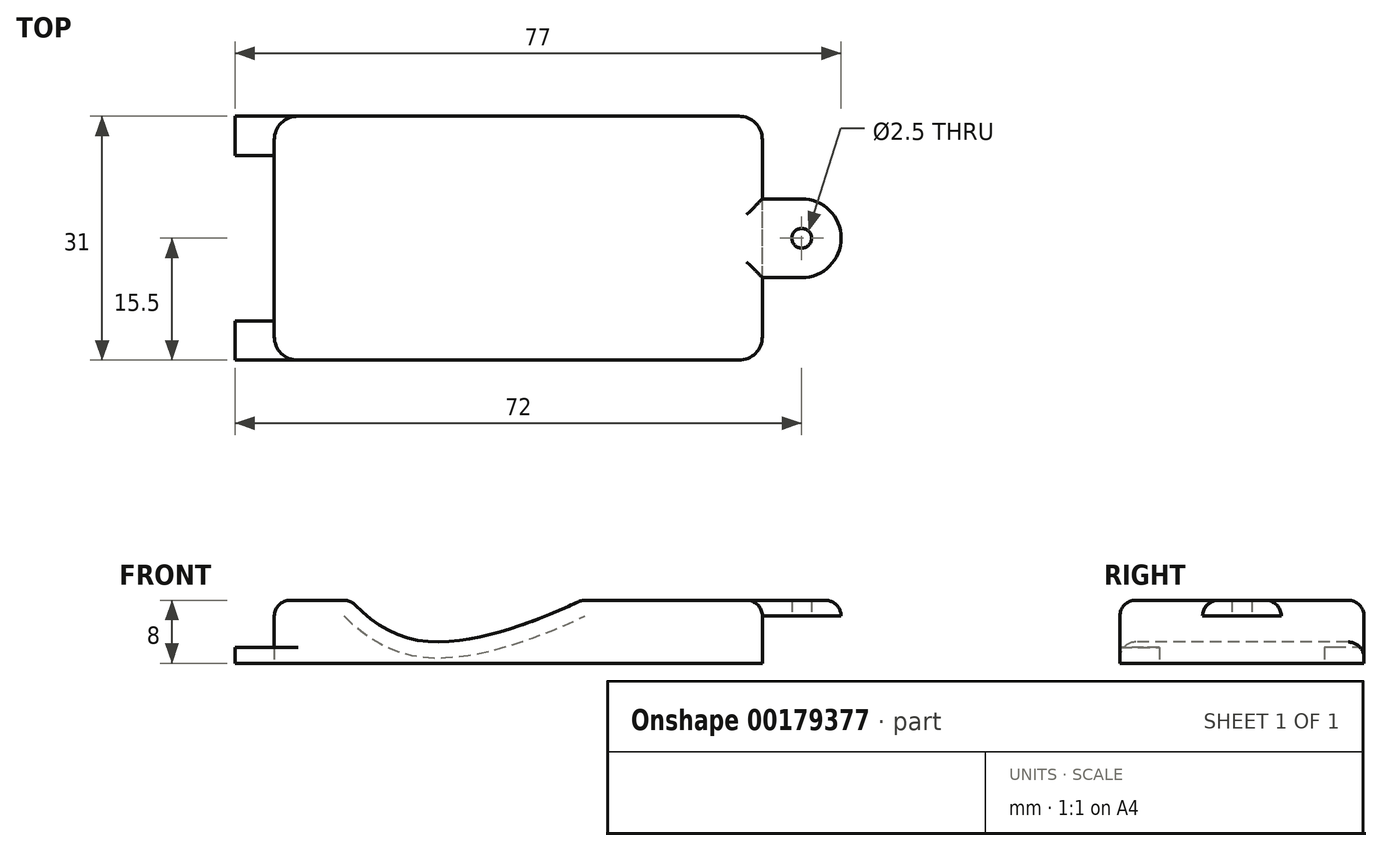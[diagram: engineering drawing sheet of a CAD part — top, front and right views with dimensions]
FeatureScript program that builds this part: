
annotation { "Feature Type Name" : "Feature", "Feature Type Description" : "" }
export const myFeature = defineFeature(function(context is Context, id is Id, definition is map)
    precondition{}
    {
        {
            var Q0;
            Q0=qCreatedBy(makeId("Top.planeOp"),FACE);
            var sketch = newSketch(context, id + "F0", { "sketchPlane" : qUnion([Q0])});
            skLineSegment(sketch, "E0.bottom", {"start": v(28, -15.5) * mm, "end": v(-31, -15.5) * mm});
            skLineSegment(sketch, "E0.top", {"start": v(28, 15.5) * mm, "end": v(-31, 15.5) * mm});
            skLineSegment(sketch, "E0.left", {"start": v(31, -12.5) * mm, "end": v(31, 12.5) * mm});
            skLineSegment(sketch, "E0.right", {"start": v(-31, -15.5) * mm, "end": v(-31, 15.5) * mm});
            skPoint(sketch, "E0.middle", {"position": v(0, 0) * mm});
            skLineSegment(sketch, "E1", {"start": v(48.88, 0) * mm, "end": v(-42.9, 0) * mm, "construction": true});
            skLineSegment(sketch, "E2.bottom", {"start": v(31, -5) * mm, "end": v(36, -5) * mm});
            skLineSegment(sketch, "E2.top", {"start": v(31, 5) * mm, "end": v(36, 5) * mm});
            skLineSegment(sketch, "E2.left", {"start": v(31, -5) * mm, "end": v(31, 5) * mm});
            skLineSegment(sketch, "E2.right", {"start": v(41, 0) * mm, "end": v(41, 0) * mm});
            skLineSegment(sketch, "E3.bottom", {"start": v(-31, 15.5) * mm, "end": v(-36, 15.5) * mm});
            skLineSegment(sketch, "E3.top", {"start": v(-31, 10.5) * mm, "end": v(-36, 10.5) * mm});
            skLineSegment(sketch, "E3.left", {"start": v(-31, 15.5) * mm, "end": v(-31, 10.5) * mm});
            skLineSegment(sketch, "E3.right", {"start": v(-36, 15.5) * mm, "end": v(-36, 10.5) * mm});
            skLineSegment(sketch, "E4.MirrorCS", {"start": v(-31, -10.5) * mm, "end": v(-36, -10.5) * mm});
            skLineSegment(sketch, "E5.MirrorCS", {"start": v(-36, -15.5) * mm, "end": v(-36, -10.5) * mm});
            skLineSegment(sketch, "E6.MirrorCS", {"start": v(-31, -15.5) * mm, "end": v(-36, -15.5) * mm});
            skPoint(sketch, "E7.visualSharp", {"position": v(41, 5) * mm});
            skArc(sketch, "E7.filletArc", {"start": v(41, 0) * mm, "mid": v(39.54, 3.54) * mm, "end": v(36, 5) * mm});
            skPoint(sketch, "E8.visualSharp", {"position": v(41, -5) * mm});
            skArc(sketch, "E8.filletArc", {"start": v(36, -5) * mm, "mid": v(39.54, -3.54) * mm, "end": v(41, 0) * mm});
            skPoint(sketch, "E9.visualSharp", {"position": v(31, 15.5) * mm});
            skArc(sketch, "E9.filletArc", {"start": v(31, 12.5) * mm, "mid": v(30.12, 14.62) * mm, "end": v(28, 15.5) * mm});
            skPoint(sketch, "E10.visualSharp", {"position": v(31, -15.5) * mm});
            skArc(sketch, "E10.filletArc", {"start": v(28, -15.5) * mm, "mid": v(30.12, -14.62) * mm, "end": v(31, -12.5) * mm});
            skCircle(sketch, "E11", {"center": v(36, 0) * mm, "radius": 1.25 * mm});
            skSolve(sketch);
        }
        {
            var Q0;
            Q0=makeQuery(id+"F0.imprint","IMPRINT",FACE,{"disambiguationData":[TD([[makeQuery(id+"F0.imprint","IMPRINT",EDGE,{"derivedFrom":sQuery(id+"F0.wireOp",EDGE,"E3.bottom")}),1.0]])]});
            var Q1;
            {var subQ3=sQuery(id+"F0.wireOp",EDGE,"E0.bottom");Q1=makeQuery(id+"F0.imprint","IMPRINT",FACE,{"disambiguationData":[TD([[makeQuery(id+"F0.imprint","IMPRINT",EDGE,{"derivedFrom":subQ3}),-1.0]])]});}
            var Q2;
            {var subQ2=sQuery(id+"F0.wireOp",EDGE,"E4.MirrorCS");Q2=makeQuery(id+"F0.imprint","IMPRINT",FACE,{"disambiguationData":[TD([[makeQuery(id+"F0.imprint","IMPRINT",EDGE,{"derivedFrom":subQ2}),1.0]])]});}
            extrude(context, id + "F1", {"entities" : qUnion([Q0, Q1, Q2]), "depth" : 2 * mm});
        }
        {
            var Q0;
            Q0=makeQuery(id+"F0.imprint","IMPRINT",FACE,{"disambiguationData":[TD([[makeQuery(id+"F0.imprint","IMPRINT",EDGE,{"derivedFrom":sQuery(id+"F0.wireOp",EDGE,"E2.bottom")}),1.0]])]});
            var Q1;
            {var subQ3=sQuery(id+"F0.wireOp",EDGE,"E0.bottom");Q1=makeQuery(id+"F0.imprint","IMPRINT",FACE,{"disambiguationData":[TD([[makeQuery(id+"F0.imprint","IMPRINT",EDGE,{"derivedFrom":subQ3}),-1.0]])]});}
            extrude(context, id + "F2", {"entities" : qUnion([Q0, Q1]), "operationType" : NewBodyOperationType.ADD, "depth" : 8 * mm});
        }
        {
            var Q0;
            Q0=makeQuery(id+"F0.imprint","IMPRINT",FACE,{"disambiguationData":[TD([[makeQuery(id+"F0.imprint","IMPRINT",EDGE,{"derivedFrom":sQuery(id+"F0.wireOp",EDGE,"E2.bottom")}),1.0]])]});
            extrude(context, id + "F3", {"entities" : qUnion([Q0]), "operationType" : NewBodyOperationType.REMOVE, "depth" : 6 * mm});
        }
        {
            var Q0;
            {var subQ0=sQuery(id+"F0.wireOp",EDGE,"E0.bottom");Q0=makeQuery(id+"F2.boolean.opBoolean","MERGE",FACE,{"derivedFrom":[makeQuery(id+"F1.opExtrude","SWEPT_FACE",FACE,{"disambiguationData":[OSD([subQ0,sQuery(id+"F0.wireOp",EDGE,"E6.MirrorCS")])]}),makeQuery(id+"F2.opExtrude","SWEPT_FACE",FACE,{"disambiguationData":[OSD([subQ0])]})]});}
            var sketch = newSketch(context, id + "F4", { "sketchPlane" : qUnion([Q0])});
            skLineSegment(sketch, "E12", {"start": v(-21.3, 14.03) * mm, "end": v(-21.3, -8.42) * mm, "construction": true});
            skLineSegment(sketch, "E13", {"start": v(-12, 14.03) * mm, "end": v(-12, -8.42) * mm, "construction": true});
            skLineSegment(sketch, "E14", {"start": v(8, 14.03) * mm, "end": v(8, -8.42) * mm, "construction": true});
            skLineSegment(sketch, "E15", {"start": v(13.95, 2.8) * mm, "end": v(42.33, 2.46) * mm, "construction": true});
            skPoint(sketch, "E15.endSnap0", {"position": v(8, 2.8) * mm});
            skFitSpline(sketch, "E16", {"points": [v(-21.3, 8) * mm, v(-12, 2.8) * mm, v(8, 8) * mm], "startDerivative": vector(19.36, -20.15) * mm, "endDerivative": vector(38.26, 18.17) * mm});
            skLineSegment(sketch, "E17", {"start": v(-21.3, 8) * mm, "end": v(8, 8) * mm});
            skSolve(sketch);
        }
        {
            var Q0;
            Q0=makeQuery(id+"F2.opExtrude","SWEPT_EDGE",EDGE,{"disambiguationData":[OSD([sQuery(id+"F0.wireOp",EDGE,"E0.top"),sQuery(id+"F0.wireOp",EDGE,"E3.bottom"),sQuery(id+"F0.wireOp",EDGE,"E3.left")])]});
            var Q1;
            Q1=makeQuery(id+"F2.opExtrude","SWEPT_EDGE",EDGE,{"disambiguationData":[OSD([sQuery(id+"F0.wireOp",EDGE,"E0.bottom"),sQuery(id+"F0.wireOp",EDGE,"E0.right"),sQuery(id+"F0.wireOp",EDGE,"E6.MirrorCS")])]});
            fillet(context, id + "F5", {"entities" : qUnion([Q0, Q1]), "radius" : 3 * mm, "tangentPropagation" : true, "allowEdgeOverflow" : false});
        }
        {
            var Q0;
            Q0=makeQuery(id+"F4.imprint","IMPRINT",FACE,{"disambiguationData":[TD([[makeQuery(id+"F4.imprint","IMPRINT",EDGE,{"derivedFrom":sQuery(id+"F4.wireOp",EDGE,"E16")}),1.0]])]});
            extrude(context, id + "F6", {"entities" : qUnion([Q0]), "operationType" : NewBodyOperationType.REMOVE, "oppositeDirection" : true, "depth" : 50 * mm});
        }
        {
            var Q0;
            Q0=makeQuery(id+"F2.opExtrude","CAP_EDGE",EDGE,{"disambiguationData":[OSD([sQuery(id+"F0.wireOp",EDGE,"E2.bottom")])],"isStart":false});
            var Q1;
            Q1=makeQuery(id+"F2.opExtrude","CAP_EDGE",EDGE,{"disambiguationData":[OSD([sQuery(id+"F0.wireOp",EDGE,"E10.filletArc")])],"isStart":false});
            var Q2;
            Q2=makeQuery(id+"F6.boolean.opBoolean","COPY",FACE,{"derivedFrom":makeQuery(id+"F6.opExtrude","SWEPT_FACE",FACE,{"disambiguationData":[OSD([sQuery(id+"F4.wireOp",EDGE,"E16")])]})});
            var Q3;
            Q3=makeQuery(id+"F2.opExtrude","CAP_EDGE",EDGE,{"disambiguationData":[OSD([sQuery(id+"F0.wireOp",EDGE,"E2.top")])],"isStart":false});
            var Q4;
            {var subQ0=sQuery(id+"F0.wireOp",EDGE,"E0.left");Q4=makeQuery(id+"F2.opExtrude","CAP_EDGE",EDGE,{"disambiguationData":[OSD([subQ0]),TDD([makeQuery(id+"F0.imprint","IMPRINT",EDGE,{"disambiguationData":[TD([[makeQuery(id+"F0.imprint","INTERSECT",VERTEX,{"derivedFrom":[subQ0,sQuery(id+"F0.wireOp",EDGE,"E9.filletArc")]}),1.0]])],"derivedFrom":subQ0})])],"isStart":false});}
            var Q5;
            Q5=makeQuery(id+"F2.opExtrude","CAP_EDGE",EDGE,{"disambiguationData":[OSD([sQuery(id+"F0.wireOp",EDGE,"E9.filletArc")])],"isStart":false});
            var Q6;
            {var subQ0=sQuery(id+"F0.wireOp",EDGE,"E0.bottom");var subQ1=sQuery(id+"F0.wireOp",EDGE,"E0.right");var subQ3=sQuery(id+"F0.wireOp",EDGE,"E0.top");var subQ5=sQuery(id+"F0.wireOp",EDGE,"E3.left");Q6=makeQuery(id+"F6.boolean.opBoolean","SPLIT",FACE,{"disambiguationData":[TD([makeQuery(id+"F1.opExtrude","SWEPT_FACE",FACE,{"disambiguationData":[OSD([subQ1])]})])],"derivedFrom":makeQuery(id+"F2.opExtrude","CAP_FACE",FACE,{"disambiguationData":[OSD([subQ0,subQ3,sQuery(id+"F0.wireOp",EDGE,"E0.left"),subQ1,sQuery(id+"F0.wireOp",EDGE,"E2.bottom"),sQuery(id+"F0.wireOp",EDGE,"E2.top"),subQ5,sQuery(id+"F0.wireOp",EDGE,"E7.filletArc"),sQuery(id+"F0.wireOp",EDGE,"E8.filletArc"),sQuery(id+"F0.wireOp",EDGE,"E9.filletArc"),sQuery(id+"F0.wireOp",EDGE,"E10.filletArc"),sQuery(id+"F0.wireOp",EDGE,"E11")])],"isStart":false})});}
            var Q7;
            {var subQ0=sQuery(id+"F0.wireOp",EDGE,"E10.filletArc");var subQ1=sQuery(id+"F0.wireOp",EDGE,"E0.bottom");Q7=makeQuery(id+"F6.boolean.opBoolean","SPLIT",EDGE,{"disambiguationData":[TD([makeQuery(id+"F1.opExtrude","SWEPT_FACE",FACE,{"disambiguationData":[OSD([subQ0])]})])],"derivedFrom":makeQuery(id+"F2.opExtrude","CAP_EDGE",EDGE,{"disambiguationData":[OSD([subQ1])],"isStart":false})});}
            var Q8;
            {var subQ0=sQuery(id+"F0.wireOp",EDGE,"E0.left");Q8=makeQuery(id+"F2.opExtrude","CAP_EDGE",EDGE,{"disambiguationData":[OSD([subQ0]),TDD([makeQuery(id+"F0.imprint","IMPRINT",EDGE,{"disambiguationData":[TD([[makeQuery(id+"F0.imprint","INTERSECT",VERTEX,{"derivedFrom":[subQ0,sQuery(id+"F0.wireOp",EDGE,"E10.filletArc")]}),-1.0]])],"derivedFrom":subQ0})])],"isStart":false});}
            var Q9;
            Q9=makeQuery(id+"F2.opExtrude","CAP_EDGE",EDGE,{"disambiguationData":[OSD([sQuery(id+"F0.wireOp",EDGE,"E7.filletArc"),sQuery(id+"F0.wireOp",EDGE,"E8.filletArc")])],"isStart":false});
            var Q10;
            {var subQ0=sQuery(id+"F0.wireOp",EDGE,"E0.top");var subQ1=sQuery(id+"F0.wireOp",EDGE,"E9.filletArc");Q10=makeQuery(id+"F6.boolean.opBoolean","SPLIT",EDGE,{"disambiguationData":[TD([makeQuery(id+"F1.opExtrude","SWEPT_FACE",FACE,{"disambiguationData":[OSD([subQ1])]})])],"derivedFrom":makeQuery(id+"F2.opExtrude","CAP_EDGE",EDGE,{"disambiguationData":[OSD([subQ0])],"isStart":false})});}
            fillet(context, id + "F7", {"entities" : qUnion([Q0, Q1, Q2, Q3, Q4, Q5, Q6, Q7, Q8, Q9, Q10]), "radius" : 2 * mm, "tangentPropagation" : true, "allowEdgeOverflow" : false});
        }
    });
